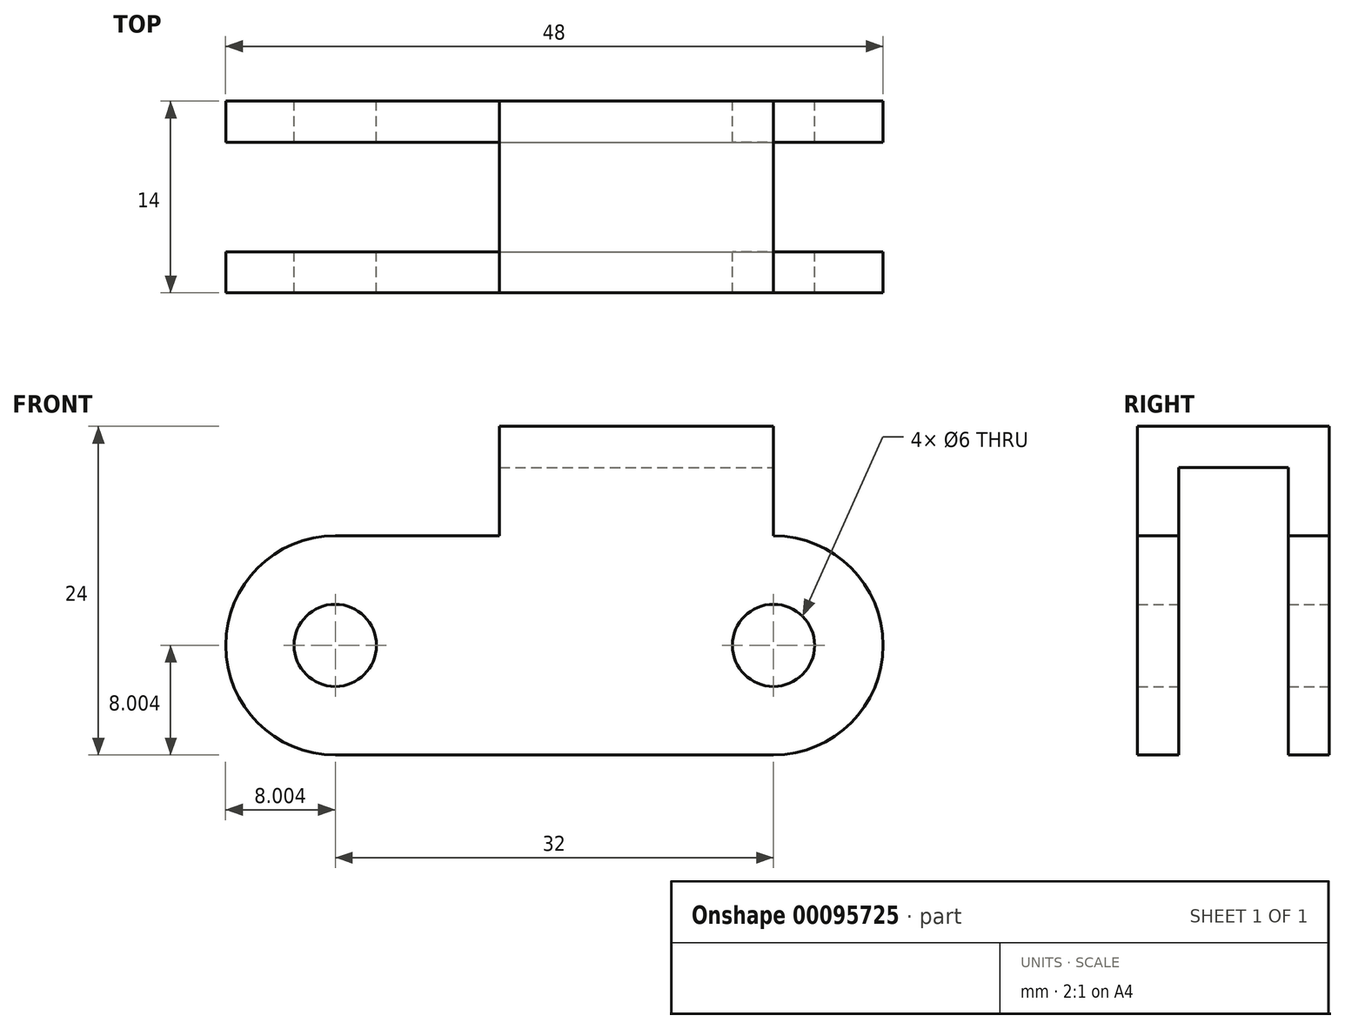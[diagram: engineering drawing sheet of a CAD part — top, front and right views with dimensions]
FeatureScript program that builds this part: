
annotation { "Feature Type Name" : "Feature", "Feature Type Description" : "" }
export const myFeature = defineFeature(function(context is Context, id is Id, definition is map)
    precondition{}
    {
        {
            var Q0;
            Q0=qCreatedBy(makeId("Front.planeOp"),FACE);
            var sketch = newSketch(context, id + "F0", { "sketchPlane" : qUnion([Q0])});
            skLineSegment(sketch, "E0", {"start": v(-13.98, -12.7) * mm, "end": v(18.02, -12.7) * mm});
            skArc(sketch, "E1", {"start": v(18.02, -12.7) * mm, "mid": v(26.02, -4.7) * mm, "end": v(18.02, 3.3) * mm});
            skArc(sketch, "E2", {"start": v(-13.98, 3.3) * mm, "mid": v(-21.98, -4.7) * mm, "end": v(-13.98, -12.7) * mm});
            skCircle(sketch, "E3", {"center": v(18.02, -4.7) * mm, "radius": 3 * mm});
            skCircle(sketch, "E4", {"center": v(-13.98, -4.7) * mm, "radius": 3 * mm});
            skLineSegment(sketch, "E5", {"start": v(-13.98, 3.3) * mm, "end": v(-1.98, 3.3) * mm});
            skLineSegment(sketch, "E6", {"start": v(-1.98, 3.3) * mm, "end": v(-1.98, 11.3) * mm});
            skLineSegment(sketch, "E7", {"start": v(-1.98, 11.3) * mm, "end": v(18.02, 11.3) * mm});
            skLineSegment(sketch, "E8", {"start": v(18.02, 11.3) * mm, "end": v(18.02, 3.3) * mm});
            skSolve(sketch);
        }
        {
            var Q0;
            Q0 = qSketchRegion(id + "F0", true);
            extrude(context, id + "F1", {"entities" : qUnion([Q0]), "depth" : 14 * mm});
        }
        {
            var Q0;
            Q0=makeQuery(id+"F1.opExtrude","SWEPT_FACE",FACE,{"disambiguationData":[OSD([sQuery(id+"F0.wireOp",EDGE,"E2")])]});
            var Q1;
            Q1=makeQuery(id+"F1.opExtrude","SWEPT_FACE",FACE,{"disambiguationData":[OSD([sQuery(id+"F0.wireOp",EDGE,"E0")])]});
            var Q2;
            Q2=makeQuery(id+"F1.opExtrude","SWEPT_FACE",FACE,{"disambiguationData":[OSD([sQuery(id+"F0.wireOp",EDGE,"E5")])]});
            var Q3;
            Q3=makeQuery(id+"F1.opExtrude","SWEPT_FACE",FACE,{"disambiguationData":[OSD([sQuery(id+"F0.wireOp",EDGE,"E6")])]});
            var Q4;
            Q4=makeQuery(id+"F1.opExtrude","SWEPT_FACE",FACE,{"disambiguationData":[OSD([sQuery(id+"F0.wireOp",EDGE,"E4")])]});
            var Q5;
            Q5=makeQuery(id+"F1.opExtrude","SWEPT_FACE",FACE,{"disambiguationData":[OSD([sQuery(id+"F0.wireOp",EDGE,"E3")])]});
            var Q6;
            Q6=makeQuery(id+"F1.opExtrude","SWEPT_FACE",FACE,{"disambiguationData":[OSD([sQuery(id+"F0.wireOp",EDGE,"E1")])]});
            var Q7;
            Q7=makeQuery(id+"F1.opExtrude","SWEPT_FACE",FACE,{"disambiguationData":[OSD([sQuery(id+"F0.wireOp",EDGE,"E8")])]});
            shell(context, id + "F2", {"entities" : qUnion([Q0, Q1, Q2, Q3, Q4, Q5, Q6, Q7]), "thickness" : 3 * mm});
        }
    });
